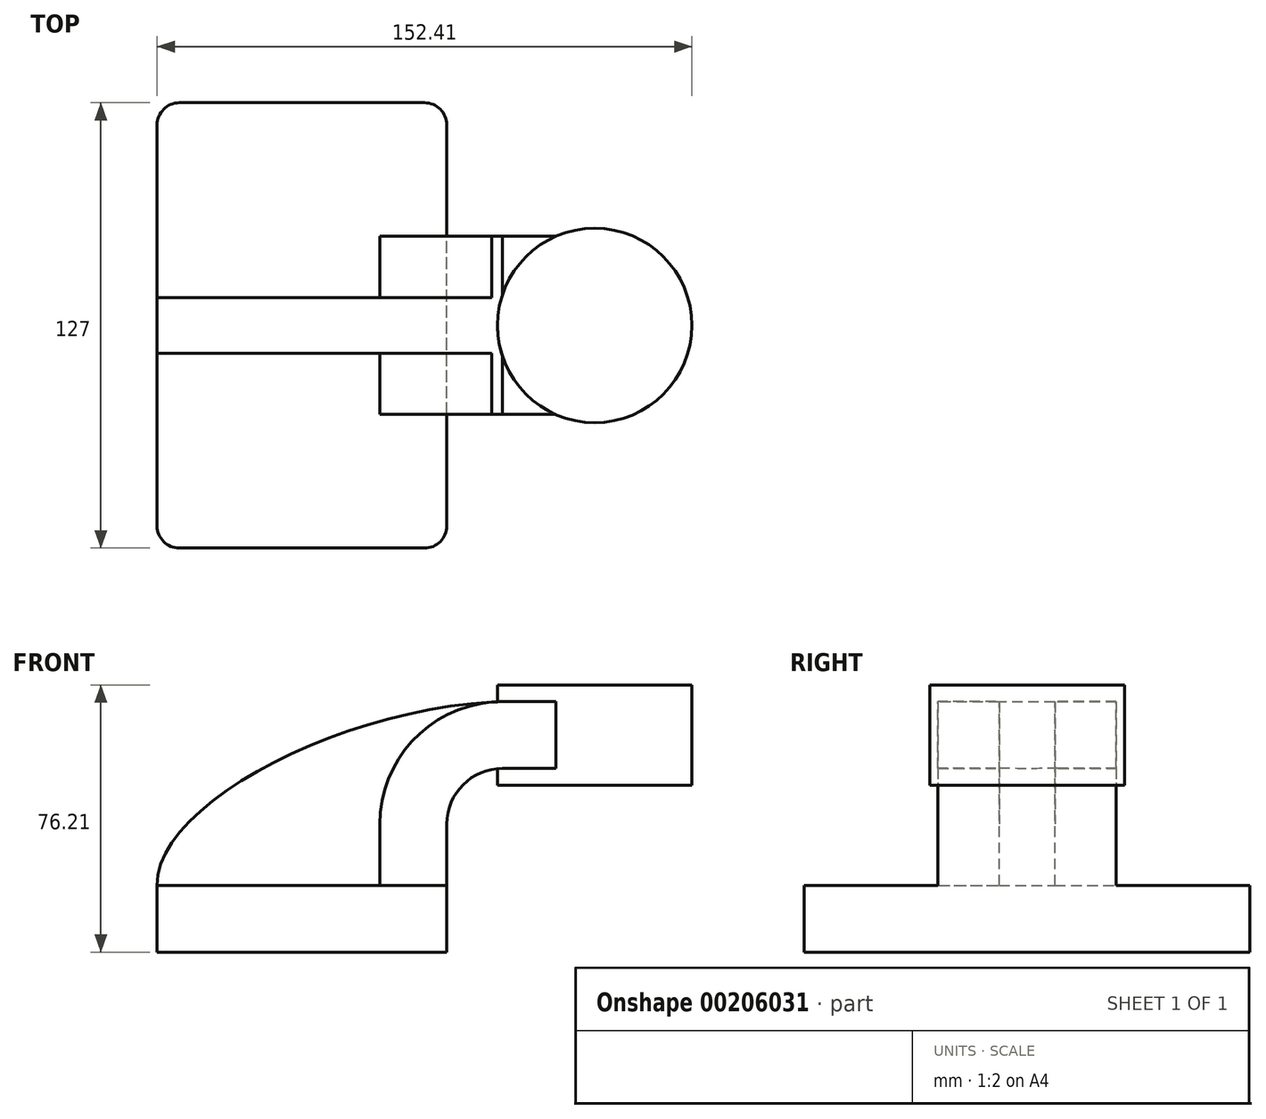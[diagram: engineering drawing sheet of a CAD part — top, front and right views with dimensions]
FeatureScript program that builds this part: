
annotation { "Feature Type Name" : "Feature", "Feature Type Description" : "" }
export const myFeature = defineFeature(function(context is Context, id is Id, definition is map)
    precondition{}
    {
        {
            var Q0;
            Q0=qCreatedBy(makeId("Front.planeOp"),FACE);
            var sketch = newSketch(context, id + "F0", { "sketchPlane" : qUnion([Q0])});
            skLineSegment(sketch, "E0.bottom", {"start": v(41.27, 9.53) * mm, "end": v(-41.28, 9.53) * mm});
            skLineSegment(sketch, "E0.top", {"start": v(41.28, -9.52) * mm, "end": v(-41.27, -9.52) * mm});
            skLineSegment(sketch, "E0.left", {"start": v(41.28, 9.53) * mm, "end": v(41.28, -9.52) * mm});
            skLineSegment(sketch, "E0.right", {"start": v(-41.28, 9.53) * mm, "end": v(-41.27, -9.52) * mm});
            skPoint(sketch, "E0.middle", {"position": v(0, 0) * mm});
            skLineSegment(sketch, "E1.bottom", {"start": v(60.32, 38.1) * mm, "end": v(111.12, 38.1) * mm});
            skLineSegment(sketch, "E1.top", {"start": v(60.32, 66.68) * mm, "end": v(111.12, 66.68) * mm});
            skLineSegment(sketch, "E1.left", {"start": v(60.32, 38.1) * mm, "end": v(60.32, 66.68) * mm});
            skLineSegment(sketch, "E1.right", {"start": v(111.12, 38.1) * mm, "end": v(111.12, 66.68) * mm});
            skPoint(sketch, "E1.middle", {"position": v(85.72, 52.39) * mm});
            skLineSegment(sketch, "E2", {"start": v(41.27, 9.53) * mm, "end": v(41.27, 26.99) * mm});
            skArc(sketch, "E3", {"start": v(41.27, 26.99) * mm, "mid": v(45.92, 38.21) * mm, "end": v(57.15, 42.86) * mm});
            skLineSegment(sketch, "E4", {"start": v(57.15, 42.86) * mm, "end": v(83.48, 42.86) * mm});
            skLineSegment(sketch, "E5.0", {"start": v(57.15, 61.91) * mm, "end": v(83.48, 61.91) * mm});
            skArc(sketch, "E5.1", {"start": v(22.23, 26.99) * mm, "mid": v(32.45, 51.68) * mm, "end": v(57.15, 61.91) * mm});
            skLineSegment(sketch, "E5.2", {"start": v(22.22, 9.53) * mm, "end": v(22.22, 26.99) * mm});
            skFitSpline(sketch, "E6", {"points": [v(-41.28, 9.52) * mm, v(57.15, 61.91) * mm], "startDerivative": vector(-0.99, 70.07) * mm, "endDerivative": vector(135.87, 4.22) * mm});
            skLineSegment(sketch, "E7", {"start": v(83.4, 66.68) * mm, "end": v(83.4, 38.1) * mm});
            skSolve(sketch);
        }
        {
            var Q0;
            Q0=makeQuery(id+"F0.imprint","IMPRINT",FACE,{"disambiguationData":[TD([[makeQuery(id+"F0.imprint","IMPRINT",EDGE,{"derivedFrom":sQuery(id+"F0.wireOp",EDGE,"E0.top")}),-1.0]])]});
            extrude(context, id + "F1", {"entities" : qUnion([Q0]), "endBound" : BoundingType.SYMMETRIC, "depth" : 127 * mm});
        }
        {
            var Q0;
            {var subQ1=sQuery(id+"F0.wireOp",EDGE,"E2");Q0=makeQuery(id+"F0.imprint","IMPRINT",FACE,{"disambiguationData":[TD([[makeQuery(id+"F0.imprint","IMPRINT",EDGE,{"derivedFrom":subQ1}),1.0]])]});}
            var Q1;
            {var subQ0=sQuery(id+"F0.wireOp",EDGE,"E4");var subQ1=sQuery(id+"F0.wireOp",EDGE,"E1.left");var subQ2=makeQuery(id+"F0.imprint","INTERSECT",VERTEX,{"derivedFrom":[subQ1,subQ0]});Q1=makeQuery(id+"F0.imprint","IMPRINT",FACE,{"disambiguationData":[TD([[makeQuery(id+"F0.imprint","IMPRINT",EDGE,{"disambiguationData":[TD([[subQ2,-1.0]])],"derivedFrom":subQ1}),-1.0]])]});}
            extrude(context, id + "F2", {"entities" : qUnion([Q0, Q1]), "operationType" : NewBodyOperationType.ADD, "endBound" : BoundingType.SYMMETRIC, "depth" : 50.8 * mm});
        }
        {
            var Q0;
            {var subQ3=sQuery(id+"F0.wireOp",EDGE,"E5.2");Q0=makeQuery(id+"F0.imprint","IMPRINT",FACE,{"disambiguationData":[TD([[makeQuery(id+"F0.imprint","IMPRINT",EDGE,{"derivedFrom":subQ3}),1.0]])]});}
            extrude(context, id + "F3", {"entities" : qUnion([Q0]), "operationType" : NewBodyOperationType.ADD, "endBound" : BoundingType.SYMMETRIC, "depth" : 15.88 * mm});
        }
        {
            var Q0;
            {var subQ0=sQuery(id+"F0.wireOp",EDGE,"E1.right");Q0=makeQuery(id+"F0.imprint","IMPRINT",FACE,{"disambiguationData":[TD([[makeQuery(id+"F0.imprint","IMPRINT",EDGE,{"derivedFrom":subQ0}),1.0]])]});}
            var Q1;
            Q1=sQuery(id+"F0.wireOp",EDGE,"E7");
            revolve(context, id + "F4", {"operationType" : NewBodyOperationType.ADD, "entities" : qUnion([Q0]), "axis" : qUnion([Q1]), "revolveType" : RevolveType.FULL});
        }
        {
            var Q0;
            Q0=makeQuery(id+"F1.opExtrude","CAP_EDGE",EDGE,{"disambiguationData":[OSD([sQuery(id+"F0.wireOp",EDGE,"E0.left")])],"isStart":false});
            var Q1;
            Q1=makeQuery(id+"F1.opExtrude","CAP_EDGE",EDGE,{"disambiguationData":[OSD([sQuery(id+"F0.wireOp",EDGE,"E0.left")])],"isStart":true});
            var Q2;
            Q2=makeQuery(id+"F1.opExtrude","CAP_EDGE",EDGE,{"disambiguationData":[OSD([sQuery(id+"F0.wireOp",EDGE,"E0.right")])],"isStart":false});
            var Q3;
            Q3=makeQuery(id+"F1.opExtrude","CAP_EDGE",EDGE,{"disambiguationData":[OSD([sQuery(id+"F0.wireOp",EDGE,"E0.right")])],"isStart":true});
            fillet(context, id + "F5", {"entities" : qUnion([Q0, Q1, Q2, Q3]), "radius" : 6.35 * mm, "tangentPropagation" : true, "allowEdgeOverflow" : false});
        }
    });
